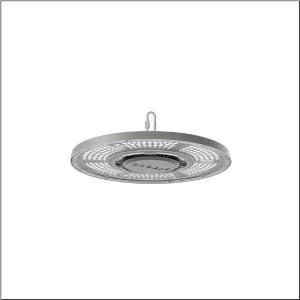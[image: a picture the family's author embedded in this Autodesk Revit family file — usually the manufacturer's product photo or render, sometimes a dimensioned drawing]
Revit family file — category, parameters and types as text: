
# Revit family: highbay_31-l_51hc42da4jmb
name_source: partatom
category: Lighting Fixtures
units: mm (PartAtom-declared; Revit-internal decimal feet)

## family parameters
Cut with Voids When Loaded = No
Host = Face
Light Source = No
Part Type = Normal
Room Calculation Point = No
Round Connector Dimension = Use Diameter
Shared = No

## types (1)
- Highbay 31-L (1 x LED, 20000 lm, 134 W, 4000K)
    Apparent Load = 134 VA
    CIE Flux Codes = 77 99 100 100 100
    Color Rendering = 80
    Color Temperature = 4000K
    Default Elevation = 1800 mm
    Description = Highbay 31-L, LED high bay luminaire, primary light control with lens, of PC, primary optical cover: cover panel, of PC, transparent, light emission: direct distribution, primary light characteristic: rotationally symmetric, installation type: suspended mounting, surface-mounted, LED, rated luminous flux: 20.000lm, luminous efficacy: 150lm/W, light colour: 840, colour temperature: 4000K, control gear: ECG DALI, with cable, 5x 1.0mm², free wire ends, mains connection: 220..240V, AC/DC, 0/50..60Hz, cable length: 1,5m, rated input power: 134W, housing, rotationally symmetric, of diecast aluminium, powder-coated, grey aluminium (RAL 9007), with hook on luminaire side, incl. screw, diameter: 404mm, protection rating (complete): IP65, insulation class (complete): insulation class I (protective earthing), certification: CE, ENEC, UKCA, protection symbol: D, impact resistance: IK08, permissible operating ambient temperature: -30..+45°C, standard: EN 60598-2-22, EN 60598, corresponds to IFS (International Featured Standards) requirements for safety and quality in the food industry, packaging unit: 1 piece
    Height = 141 mm
    Lamp = 1 x LED
    Lamp Light Flux = 20000 lm
    Lamp Power = 134 W
    Lamp count = 1
    Length = 406 mm
    Luminous efficacy = 149 lm/W
    Manufacturer = Siteco
    ModVariant = No
    Model = 51HC42DA4JMB
    Mounting Place = Ceiling
    Mounting Type = Pendant
    Number of Poles = 1
    OnlyDefault = Yes
    Power Factor = 1
    Product Name = Highbay 31-L
    Product group = LED high bay luminaire
    ProductGroupID = 903
    Protection Class = Protection class I
    Protection Degree = IP 65
    RLX_Detail_Level = 1
    RLX_Emergency_Light_Flux = 0 lm
    RLX_Emergency_Type = 0
    RLX_Emergency_Type_DB = No
    RlxData = <blob elided: 162337 chars, md5=b2638611>
    Socket = socket
    Standby Power = 0 W
    System Light Flux = 20000 lm
    System Power = 134 W
    Type Comments = Product without accessories
    Type Image = l_1007237.jpg
    URL = http://relux.com
    VarID = ---
    Voltage = 0 V
    Weight = 0.00 kg
    Width = 0 mm  [stored 0 ft]

note: [stored X ft] marks values corroborated as IEEE doubles in the binary element streams (Revit-internal decimal feet)

## geometry (parser evidence)
native form markers: Blend x4, Sweep x9
no freeform markers — native parametric forms only
